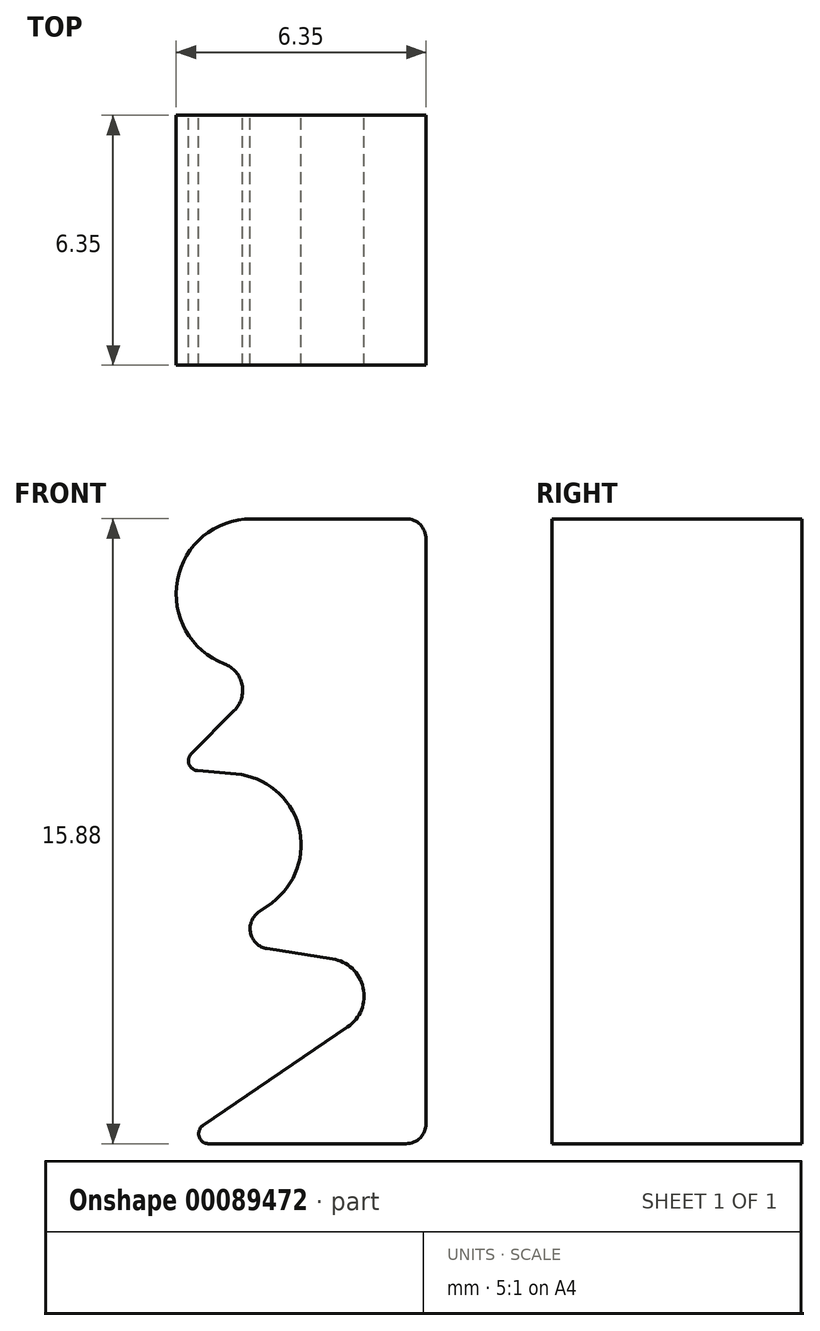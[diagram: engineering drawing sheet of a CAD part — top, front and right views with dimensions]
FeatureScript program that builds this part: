
annotation { "Feature Type Name" : "Feature", "Feature Type Description" : "" }
export const myFeature = defineFeature(function(context is Context, id is Id, definition is map)
    precondition{}
    {
        {
            var Q0;
            Q0=qCreatedBy(makeId("Front.planeOp"),FACE);
            var sketch = newSketch(context, id + "F0", { "sketchPlane" : qUnion([Q0])});
            skLineSegment(sketch, "E0.bottom", {"start": v(-0.5, 0) * mm, "end": v(-5.52, 0) * mm});
            skLineSegment(sketch, "E0.top", {"start": v(-0.5, 15.88) * mm, "end": v(-6.35, 15.88) * mm});
            skLineSegment(sketch, "E0.left", {"start": v(0, 0.5) * mm, "end": v(0, 15.37) * mm});
            skLineSegment(sketch, "E0.right", {"start": v(-6.35, 0) * mm, "end": v(-6.35, 15.88) * mm, "construction": true});
            skLineSegment(sketch, "E1", {"start": v(-6.35, 15.88) * mm, "end": v(0, 0) * mm, "construction": true});
            skLineSegment(sketch, "E2", {"start": v(0, 15.88) * mm, "end": v(-4.87, 11) * mm, "construction": true});
            skLineSegment(sketch, "E3", {"start": v(-5.8, 9.48) * mm, "end": v(-4.83, 9.4) * mm});
            skLineSegment(sketch, "E4", {"start": v(-3.92, 6.12) * mm, "end": v(-4.26, 5.87) * mm});
            skLineSegment(sketch, "E5", {"start": v(-4.04, 4.96) * mm, "end": v(-2.38, 4.7) * mm});
            skLineSegment(sketch, "E6", {"start": v(-2, 2.96) * mm, "end": v(-5.67, 0.46) * mm});
            skArc(sketch, "E7", {"start": v(-4.45, 15.88) * mm, "mid": v(-6.32, 14.32) * mm, "end": v(-5.13, 12.2) * mm});
            skArc(sketch, "E8", {"start": v(-4.87, 11) * mm, "mid": v(-4.68, 11.66) * mm, "end": v(-5.13, 12.2) * mm});
            skPoint(sketch, "E9.visualSharp", {"position": v(-6.35, 9.52) * mm});
            skArc(sketch, "E9.filletArc", {"start": v(-5.96, 9.91) * mm, "mid": v(-6.02, 9.64) * mm, "end": v(-5.8, 9.48) * mm});
            skPoint(sketch, "E10.visualSharp", {"position": v(0, 8.97) * mm});
            skArc(sketch, "E10.filletArc", {"start": v(-3.92, 6.12) * mm, "mid": v(-3.24, 8.07) * mm, "end": v(-4.83, 9.4) * mm});
            skPoint(sketch, "E11.visualSharp", {"position": v(0, 4.32) * mm});
            skArc(sketch, "E11.filletArc", {"start": v(-2, 2.96) * mm, "mid": v(-1.6, 3.96) * mm, "end": v(-2.38, 4.7) * mm});
            skArc(sketch, "E12.filletArc", {"start": v(-4.26, 5.87) * mm, "mid": v(-4.46, 5.34) * mm, "end": v(-4.04, 4.96) * mm});
            skPoint(sketch, "E13.visualSharp", {"position": v(0, 15.88) * mm});
            skArc(sketch, "E13.filletArc", {"start": v(0, 15.37) * mm, "mid": v(-0.15, 15.73) * mm, "end": v(-0.5, 15.88) * mm});
            skPoint(sketch, "E14.visualSharp", {"position": v(0, 0) * mm});
            skArc(sketch, "E14.filletArc", {"start": v(-0.5, 0) * mm, "mid": v(-0.15, 0.15) * mm, "end": v(0, 0.5) * mm});
            skPoint(sketch, "E15.visualSharp", {"position": v(-6.35, 0) * mm});
            skArc(sketch, "E15.filletArc", {"start": v(-5.67, 0.46) * mm, "mid": v(-5.77, 0.18) * mm, "end": v(-5.52, 0) * mm});
            skLineSegment(sketch, "E16", {"start": v(-4.87, 11) * mm, "end": v(-5.96, 9.91) * mm});
            skSolve(sketch);
        }
        {
            var Q0;
            Q0=makeQuery(id+"F0.imprint","IMPRINT",FACE,{"disambiguationData":[TD([[makeQuery(id+"F0.imprint","IMPRINT",EDGE,{"derivedFrom":sQuery(id+"F0.wireOp",EDGE,"E0.bottom")}),-1.0]])]});
            extrude(context, id + "F1", {"entities" : qUnion([Q0]), "depth" : 6.35 * mm});
        }
    });
